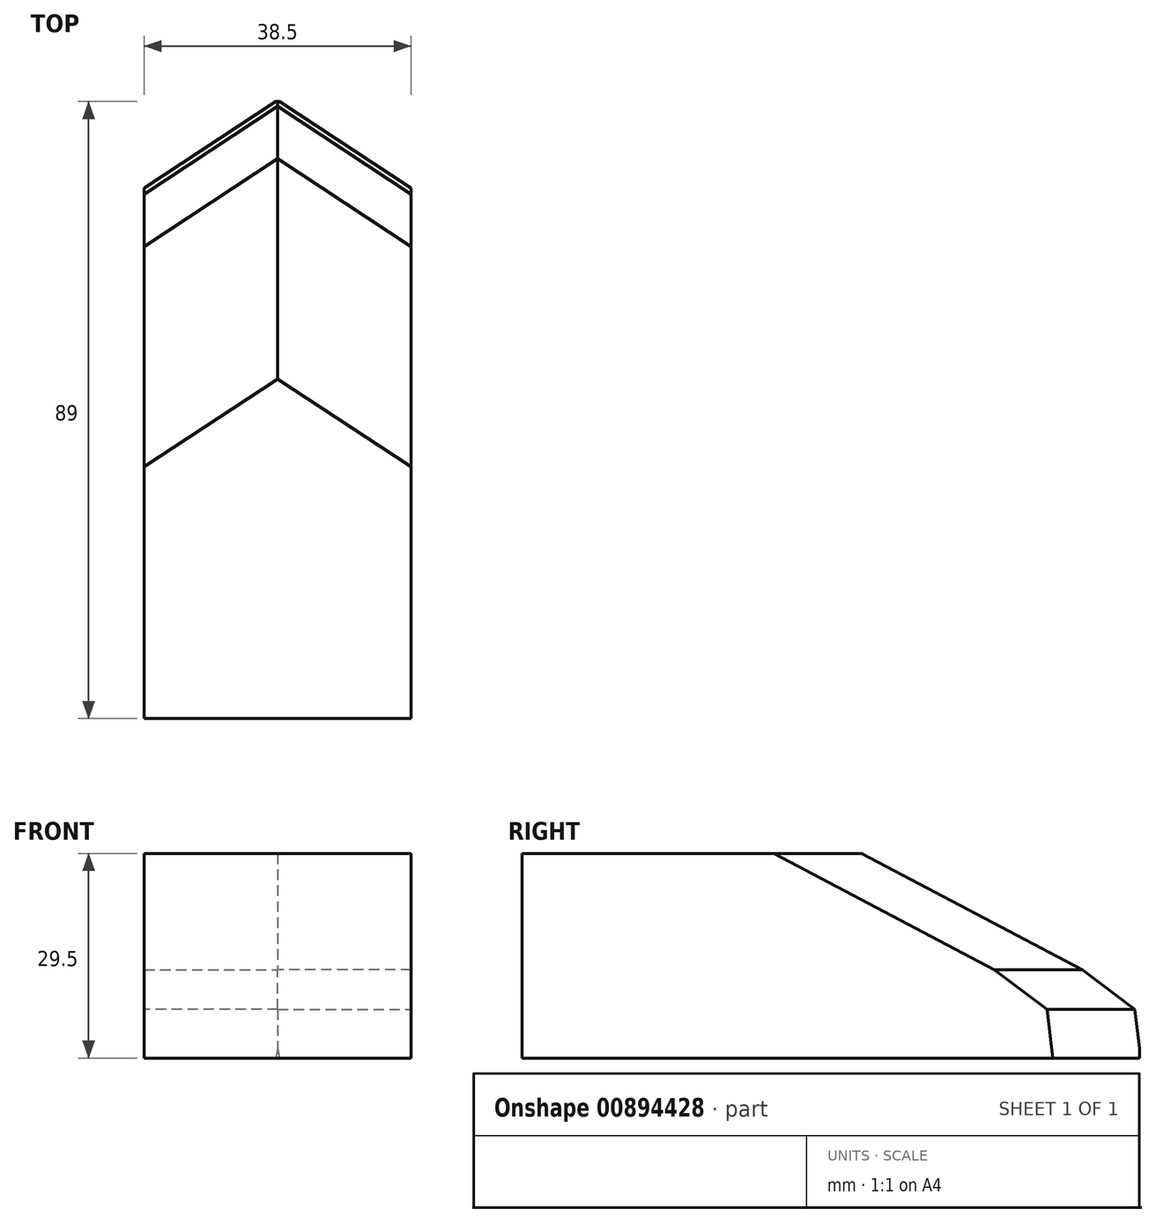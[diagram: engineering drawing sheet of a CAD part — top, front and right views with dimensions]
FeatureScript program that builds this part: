
annotation { "Feature Type Name" : "Feature", "Feature Type Description" : "" }
export const myFeature = defineFeature(function(context is Context, id is Id, definition is map)
    precondition{}
    {
        {
            var Q0;
            Q0=qCreatedBy(makeId("Top.planeOp"),FACE);
            var sketch = newSketch(context, id + "F0", { "sketchPlane" : qUnion([Q0])});
            skLineSegment(sketch, "E0.bottom", {"start": v(0, 43.68) * mm, "end": v(19.25, 43.68) * mm});
            skLineSegment(sketch, "E0.top", {"start": v(0, -45.32) * mm, "end": v(19.25, -45.32) * mm});
            skLineSegment(sketch, "E0.left", {"start": v(0, 43.68) * mm, "end": v(0, -45.32) * mm});
            skLineSegment(sketch, "E0.right", {"start": v(19.25, 43.68) * mm, "end": v(19.25, -45.32) * mm});
            skSolve(sketch);
        }
        {
            var Q0;
            Q0=makeQuery(id+"F0.imprint","IMPRINT",FACE,{"disambiguationData":[TD([[makeQuery(id+"F0.imprint","IMPRINT",EDGE,{"derivedFrom":sQuery(id+"F0.wireOp",EDGE,"E0.bottom")}),-1.0]])]});
            extrude(context, id + "F1", {"entities" : qUnion([Q0]), "depth" : 29.5 * mm, "offsetDistance" : 25 * mm});
        }
        {
            var Q0;
            Q0=makeQuery(id+"F1.opExtrude","SWEPT_EDGE",EDGE,{"disambiguationData":[OSD([sQuery(id+"F0.wireOp",EDGE,"E0.bottom"),sQuery(id+"F0.wireOp",EDGE,"E0.right")])]});
            chamfer(context, id + "F2", {"entities" : qUnion([Q0]), "chamferType" : ChamferType.TWO_OFFSETS, "width1" : 19 * mm, "oppositeDirection" : false, "width2" : 12.5 * mm, "tangentPropagation" : true});
        }
        {
            var Q0;
            {var subQ0=sQuery(id+"F0.wireOp",EDGE,"E0.right");var subQ1=sQuery(id+"F0.wireOp",EDGE,"E0.bottom");Q0=makeQuery(id+"F2.opChamfer","BLEND_EDGE",EDGE,{"blendedFrom":[makeQuery(id+"F1.opExtrude","SWEPT_EDGE",EDGE,{"disambiguationData":[OSD([subQ1,subQ0])]}),makeQuery(id+"F1.opExtrude","CAP_FACE",FACE,{"disambiguationData":[OSD([subQ1,sQuery(id+"F0.wireOp",EDGE,"E0.top"),sQuery(id+"F0.wireOp",EDGE,"E0.left"),subQ0])],"isStart":false})],"blendedInto":[makeQuery(id+"F1.opExtrude","CAP_FACE",FACE,{"disambiguationData":[OSD([subQ1,sQuery(id+"F0.wireOp",EDGE,"E0.top"),sQuery(id+"F0.wireOp",EDGE,"E0.left"),subQ0])],"isStart":false})]});}
            chamfer(context, id + "F3", {"entities" : qUnion([Q0]), "chamferType" : ChamferType.TWO_OFFSETS, "width1" : 3 * mm, "oppositeDirection" : false, "width2" : 29.5 * mm, "tangentPropagation" : true});
        }
        {
            var Q0;
            {var subQ0=sQuery(id+"F0.wireOp",EDGE,"E0.right");var subQ1=sQuery(id+"F0.wireOp",EDGE,"E0.bottom");var subQ2=makeQuery(id+"F1.opExtrude","CAP_FACE",FACE,{"disambiguationData":[OSD([subQ1,sQuery(id+"F0.wireOp",EDGE,"E0.top"),sQuery(id+"F0.wireOp",EDGE,"E0.left"),subQ0])],"isStart":false});Q0=makeQuery(id+"F3.opChamfer","BLEND_EDGE",EDGE,{"blendedFrom":[makeQuery(id+"F2.opChamfer","BLEND_EDGE",EDGE,{"blendedFrom":[makeQuery(id+"F1.opExtrude","SWEPT_EDGE",EDGE,{"disambiguationData":[OSD([subQ1,subQ0])]}),subQ2],"blendedInto":[subQ2]}),subQ2],"blendedInto":[subQ2]});}
            chamfer(context, id + "F4", {"entities" : qUnion([Q0]), "width" : 25 * mm, "tangentPropagation" : true});
        }
        {
            var Q0;
            {var subQ0=sQuery(id+"F0.wireOp",EDGE,"E0.right");var subQ1=sQuery(id+"F0.wireOp",EDGE,"E0.bottom");var subQ2=makeQuery(id+"F1.opExtrude","CAP_FACE",FACE,{"disambiguationData":[OSD([subQ1,sQuery(id+"F0.wireOp",EDGE,"E0.top"),sQuery(id+"F0.wireOp",EDGE,"E0.left"),subQ0])],"isStart":false});var subQ3=subQ2;Q0=makeQuery(id+"F4.opChamfer","BLEND_EDGE",EDGE,{"blendedFrom":[makeQuery(id+"F3.opChamfer","BLEND_EDGE",EDGE,{"blendedFrom":[makeQuery(id+"F2.opChamfer","BLEND_EDGE",EDGE,{"blendedFrom":[makeQuery(id+"F1.opExtrude","SWEPT_EDGE",EDGE,{"disambiguationData":[OSD([subQ1,subQ0])]}),subQ2],"blendedInto":[subQ2]}),subQ3],"blendedInto":[subQ3]}),subQ3],"blendedInto":[subQ3]});}
            chamfer(context, id + "F5", {"entities" : qUnion([Q0]), "chamferType" : ChamferType.TWO_OFFSETS, "width1" : 8 * mm, "oppositeDirection" : false, "width2" : 25 * mm, "tangentPropagation" : true});
        }
        {
            var Q0;
            Q0=makeQuery(id+"F1.opExtrude","SWEPT_BODY",BODY,{"disambiguationData":[OSD([sQuery(id+"F0.wireOp",EDGE,"E0.bottom"),sQuery(id+"F0.wireOp",EDGE,"E0.top"),sQuery(id+"F0.wireOp",EDGE,"E0.left"),sQuery(id+"F0.wireOp",EDGE,"E0.right")])]});
            var Q1;
            Q1=qCreatedBy(makeId("Right.planeOp"),FACE);
            mirror(context, id + "F6", {"operationType" : NewBodyOperationType.ADD, "entities" : qUnion([Q0]), "mirrorPlane" : qUnion([Q1])});
        }
    });
